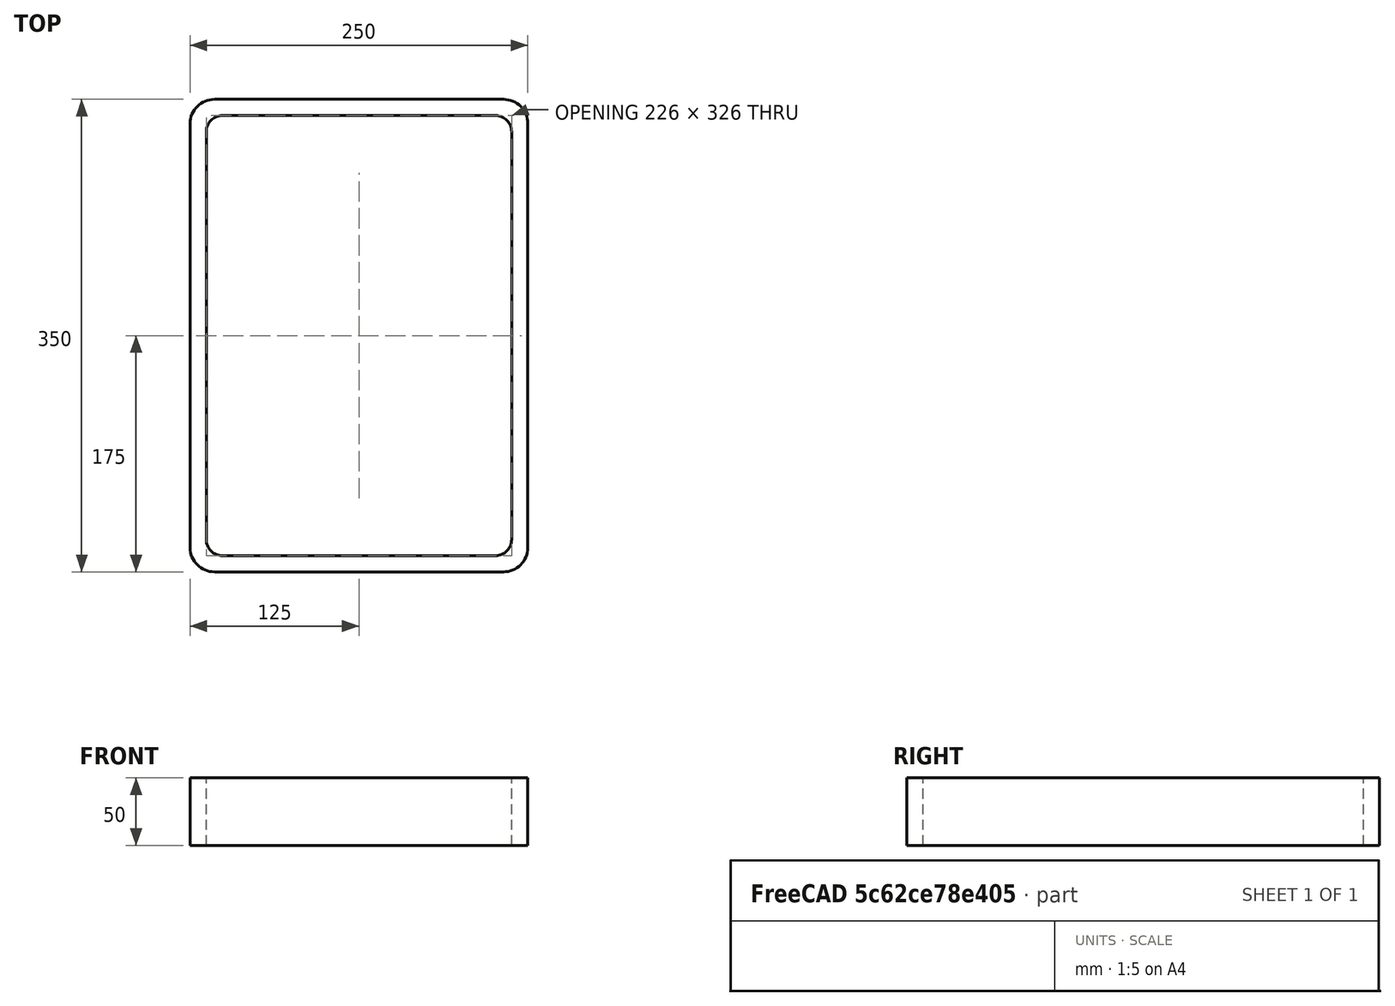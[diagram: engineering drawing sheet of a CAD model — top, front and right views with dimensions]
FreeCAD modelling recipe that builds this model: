
FCSTD DOCUMENT  (FreeCAD 0.15R4671 (Git))
Label: Rectangular hollow section 350 x250x12 EN10219 S235JRH
License: All rights reserved
LicenseURL: http://en.wikipedia.org/wiki/All_rights_reserved
objects: Sketcher::SketchObject×1, Part::Extrusion×1
note: 2 computed .brp shape members not serialized (recipe doc carries the construction recipe); baked Part::Feature solids carry a one-line shape summary decoded from their .brp

FEATURE [Sketcher::SketchObject] Sketch
  sketch-geometry (16):
    g0: LineSegment StartX=-101 StartY=163 StartZ=0 EndX=101 EndY=163 EndZ=0
    g1: LineSegment StartX=113 StartY=151 StartZ=0 EndX=113 EndY=-151 EndZ=0
    g2: LineSegment StartX=101 StartY=-163 StartZ=0 EndX=-101 EndY=-163 EndZ=0
    g3: LineSegment StartX=-113 StartY=-151 StartZ=0 EndX=-113 EndY=151 EndZ=0
    g4: LineSegment StartX=-107 StartY=175 StartZ=0 EndX=107 EndY=175 EndZ=0
    g5: LineSegment StartX=125 StartY=157 StartZ=0 EndX=125 EndY=-157 EndZ=0
    g6: LineSegment StartX=107 StartY=-175 StartZ=0 EndX=-107 EndY=-175 EndZ=0
    g7: LineSegment StartX=-125 StartY=-157 StartZ=0 EndX=-125 EndY=157 EndZ=0
    g8: ArcOfCircle CenterX=-101 CenterY=151 CenterZ=0 NormalX=0 NormalY=0 NormalZ=1 Radius=12 StartAngle=1.5708 EndAngle=3.14159
    g9: ArcOfCircle CenterX=101 CenterY=151 CenterZ=0 NormalX=0 NormalY=0 NormalZ=1 Radius=12 StartAngle=0 EndAngle=1.5708
    g10: ArcOfCircle CenterX=101 CenterY=-151 CenterZ=0 NormalX=0 NormalY=0 NormalZ=1 Radius=12 StartAngle=4.71239 EndAngle=6.28319
    g11: ArcOfCircle CenterX=-101 CenterY=-151 CenterZ=0 NormalX=0 NormalY=0 NormalZ=1 Radius=12 StartAngle=3.14159 EndAngle=4.71239
    g12: ArcOfCircle CenterX=107 CenterY=157 CenterZ=0 NormalX=0 NormalY=0 NormalZ=1 Radius=18 StartAngle=0 EndAngle=1.5708
    g13: ArcOfCircle CenterX=107 CenterY=-157 CenterZ=0 NormalX=0 NormalY=0 NormalZ=1 Radius=18 StartAngle=4.71239 EndAngle=6.28319
    g14: ArcOfCircle CenterX=-107 CenterY=-157 CenterZ=0 NormalX=0 NormalY=0 NormalZ=1 Radius=18 StartAngle=3.14159 EndAngle=4.71239
    g15: ArcOfCircle CenterX=-107 CenterY=157 CenterZ=0 NormalX=0 NormalY=0 NormalZ=1 Radius=18 StartAngle=1.5708 EndAngle=3.14159
  constraints (36):
    c: Horizontal(g2)
    c: Vertical(g3)
    c: Horizontal(g6)
    c: Vertical(g7)
    c: Tangent(g3,g8) = 1.5708
    c: Tangent(g0,g8) = 1.5708
    c: Tangent(g0,g9) = 1.5708
    c: Tangent(g1,g9) = 1.5708
    c: Tangent(g1,g10) = 1.5708
    c: Tangent(g2,g10) = 1.5708
    c: Tangent(g2,g11) = 1.5708
    c: Tangent(g3,g11) = 1.5708
    c: Tangent(g4,g12) = 1.5708
    c: Tangent(g5,g12) = 1.5708
    c: Tangent(g5,g13) = 1.5708
    c: Tangent(g6,g13) = 1.5708
    c: Tangent(g6,g14) = 1.5708
    c: Tangent(g7,g14) = 1.5708
    c: Tangent(g7,g15) = 1.5708
    c: Tangent(g4,g15) = 1.5708
    c: Equal(g9,g8)
    c: Equal(g9,g11)
    c: Equal(g9,g10)
    c: Equal(g12,g15)
    c: Equal(g12,g14)
    c: Equal(g12,g13)
    c: Symmetric(g4,g6,g-1)
    c: Symmetric(g7,g5,g-2)
    c: DistanceY(g4,g6) = -350
    c: DistanceX(g7,g5) = 250
    c: Symmetric(g3,g1,g-2)
    c: Symmetric(g0,g2,g-1)
    c: DistanceY(g0,g4) = 12
    c: DistanceX(g5,g1) = -12
    c: Radius(g9) = 12
    c: Radius(g12) = 18
FEATURE [Part::Extrusion] Extrude  label="Rectangular hollow section 350 x250x12 EN10219 S235JRH"
  Base = -> Sketch
  Dir = (0,0,50)
  Solid = true
